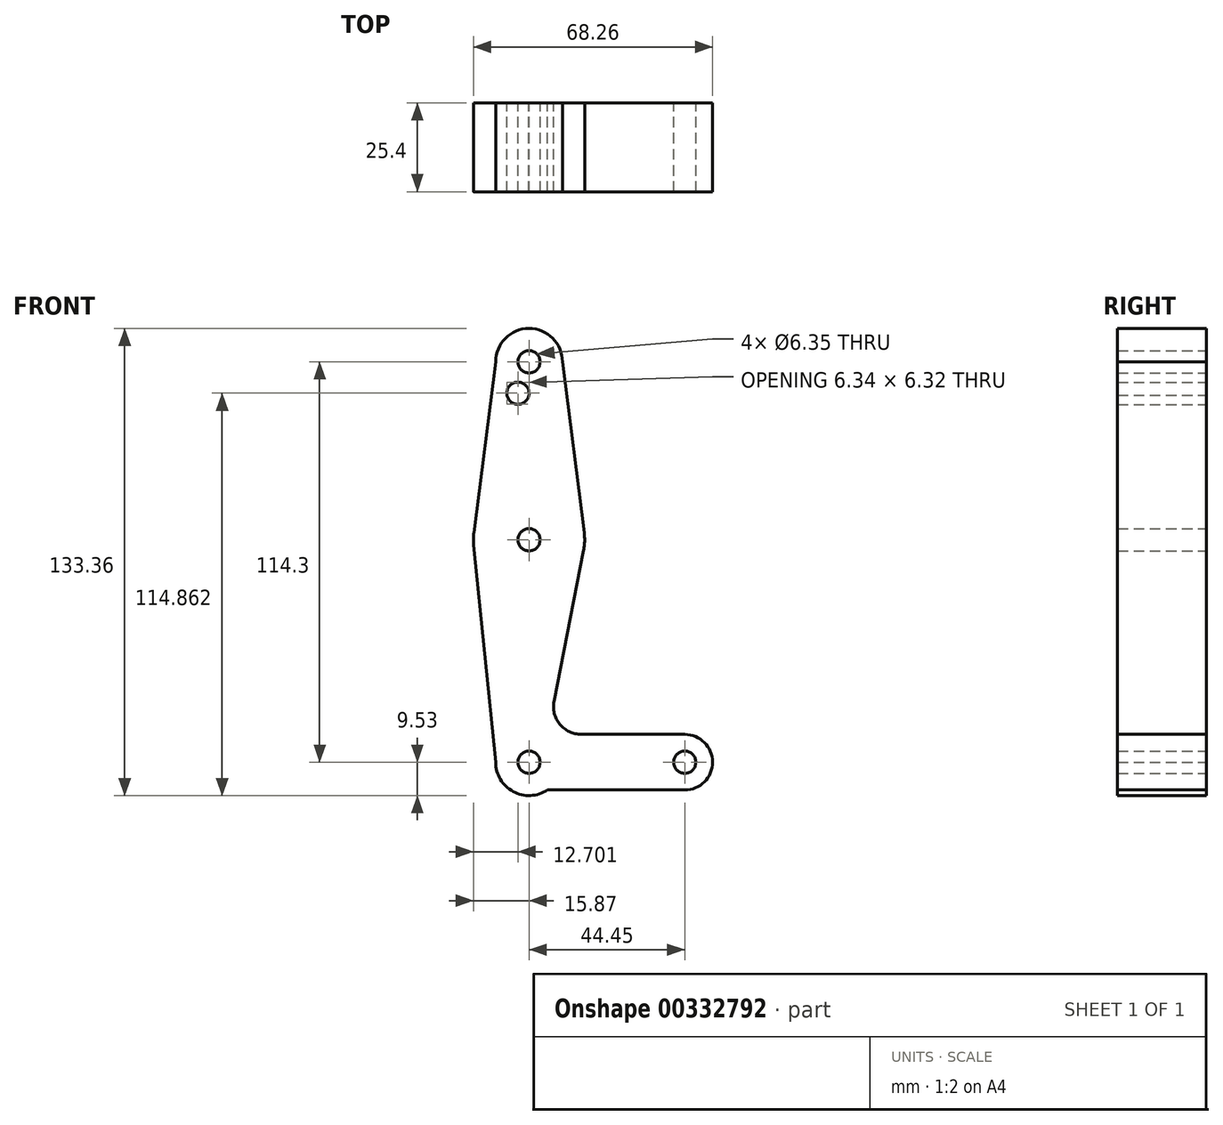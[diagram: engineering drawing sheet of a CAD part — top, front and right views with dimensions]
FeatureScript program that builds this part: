
annotation { "Feature Type Name" : "Feature", "Feature Type Description" : "" }
export const myFeature = defineFeature(function(context is Context, id is Id, definition is map)
    precondition{}
    {
        {
            var Q0;
            Q0=qCreatedBy(makeId("Front.planeOp"),FACE);
            var sketch = newSketch(context, id + "F0", { "sketchPlane" : qUnion([Q0])});
            skLineSegment(sketch, "E0", {"start": v(0, 0) * mm, "end": v(0, 114.3) * mm});
            skLineSegment(sketch, "E1", {"start": v(0, 0) * mm, "end": v(44.45, 0) * mm});
            skCircle(sketch, "E2", {"center": v(0, 0) * mm, "radius": 9.53 * mm});
            skCircle(sketch, "E3", {"center": v(44.45, 0) * mm, "radius": 7.94 * mm});
            skCircle(sketch, "E4", {"center": v(0, 63.5) * mm, "radius": 15.88 * mm});
            skCircle(sketch, "E5", {"center": v(0, 114.3) * mm, "radius": 9.53 * mm});
            skLineSegment(sketch, "E6", {"start": v(-9.53, 114.3) * mm, "end": v(-15.75, 65.5) * mm});
            skLineSegment(sketch, "E7", {"start": v(9.53, 114.3) * mm, "end": v(15.75, 65.5) * mm});
            skLineSegment(sketch, "E8", {"start": v(15.58, 60.44) * mm, "end": v(7.13, 17.42) * mm});
            skLineSegment(sketch, "E9", {"start": v(14.93, 7.94) * mm, "end": v(44.45, 7.94) * mm});
            skLineSegment(sketch, "E10", {"start": v(5.27, -7.94) * mm, "end": v(44.45, -7.94) * mm});
            skPoint(sketch, "E11.visualSharp", {"position": v(5.27, 7.94) * mm});
            skArc(sketch, "E11.filletArc", {"start": v(7.13, 17.42) * mm, "mid": v(8.79, 10.84) * mm, "end": v(14.93, 7.94) * mm});
            skCircle(sketch, "E12", {"center": v(0, 114.3) * mm, "radius": 3.18 * mm});
            skCircle(sketch, "E13", {"center": v(0, 63.5) * mm, "radius": 3.18 * mm});
            skCircle(sketch, "E14", {"center": v(0, 0) * mm, "radius": 3.18 * mm});
            skCircle(sketch, "E15", {"center": v(44.45, 0) * mm, "radius": 3.18 * mm});
            skLineSegment(sketch, "E16", {"start": v(-15.8, 61.9) * mm, "end": v(-9.52, 0) * mm});
            skCircle(sketch, "E17", {"center": v(-3.18, 105.32) * mm, "radius": 3.18 * mm});
            skSolve(sketch);
        }
        {
            var Q0;
            Q0 = qSketchRegion(id + "F0", true);
            var Q1;
            {var subQ0=sQuery(id+"F0.wireOp",EDGE,"E14");var subQ1=sQuery(id+"F0.wireOp",EDGE,"E0");var subQ2=makeQuery(id+"F0.imprint","INTERSECT",VERTEX,{"derivedFrom":[subQ1,subQ0]});Q1=makeQuery(id+"F0.imprint","IMPRINT",FACE,{"disambiguationData":[TD([[makeQuery(id+"F0.imprint","IMPRINT",EDGE,{"disambiguationData":[TD([[subQ2,-1.0]])],"derivedFrom":subQ1}),-1.0]])]});}
            extrude(context, id + "F1", {"entities" : qUnion([Q0, Q1]), "depth" : 25.4 * mm});
        }
    });
